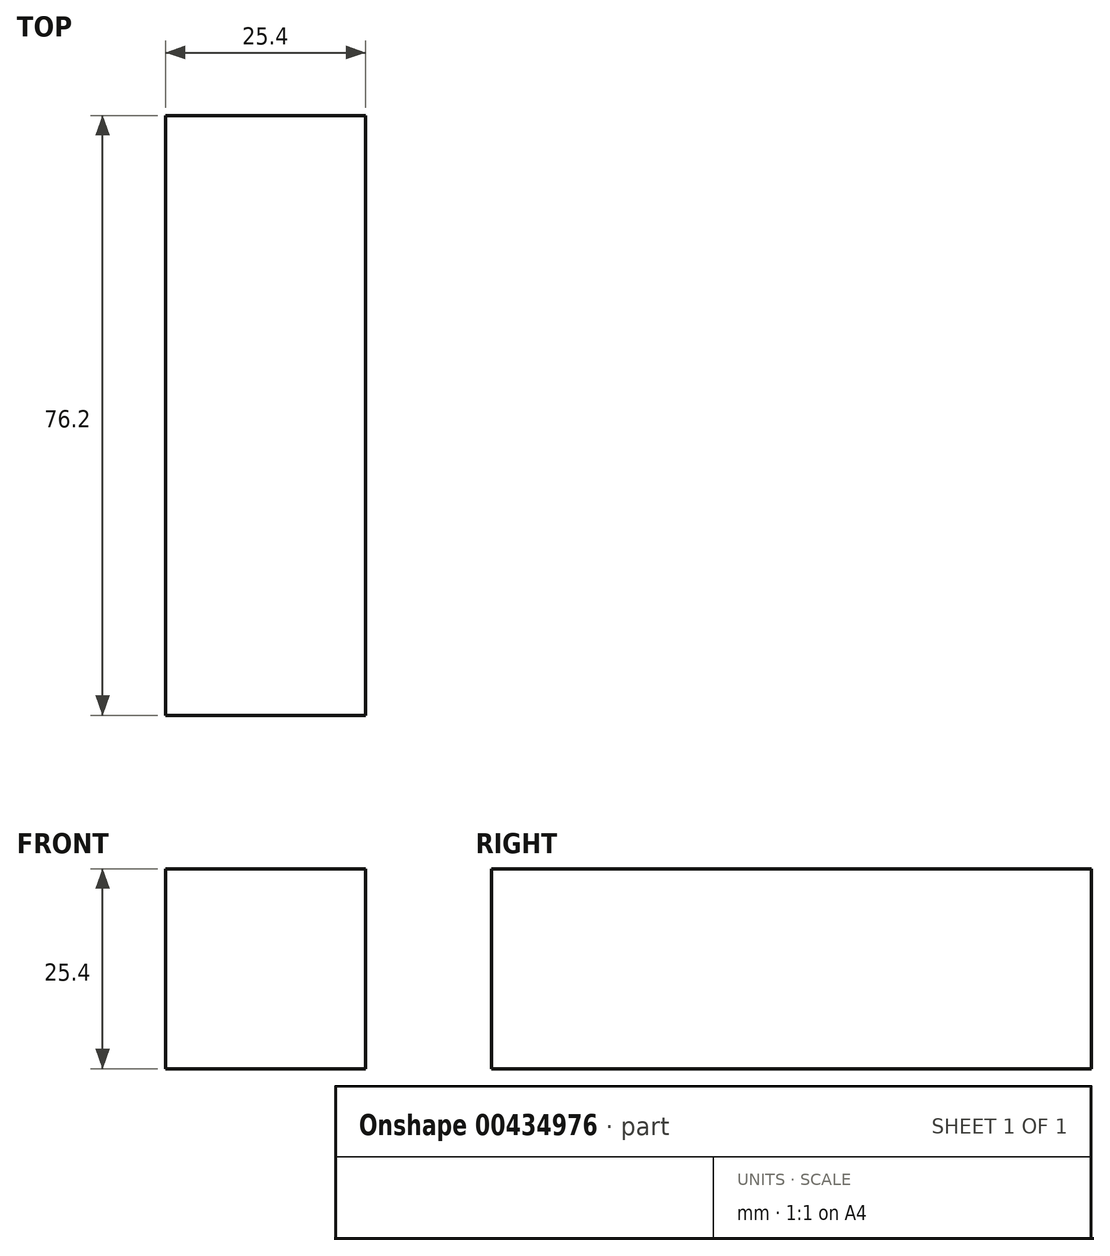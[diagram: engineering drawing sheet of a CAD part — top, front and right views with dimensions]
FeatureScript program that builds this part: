
annotation { "Feature Type Name" : "Feature", "Feature Type Description" : "" }
export const myFeature = defineFeature(function(context is Context, id is Id, definition is map)
    precondition{}
    {
        {
            var Q0;
            Q0=qCreatedBy(makeId("Front.planeOp"),FACE);
            var sketch = newSketch(context, id + "F0", { "sketchPlane" : qUnion([Q0])});
            skLineSegment(sketch, "E0", {"start": v(0, 0) * mm, "end": v(-25.4, 0) * mm});
            skLineSegment(sketch, "E1", {"start": v(-25.4, 0) * mm, "end": v(-25.4, 25.4) * mm});
            skLineSegment(sketch, "E2", {"start": v(-25.4, 25.4) * mm, "end": v(0, 25.4) * mm});
            skLineSegment(sketch, "E3", {"start": v(0, 25.4) * mm, "end": v(0, 0) * mm});
            skSolve(sketch);
        }
        {
            var Q0;
            Q0=makeQuery(id+"F0.imprint","IMPRINT",FACE,{"disambiguationData":[TD([[makeQuery(id+"F0.imprint","IMPRINT",EDGE,{"derivedFrom":sQuery(id+"F0.wireOp",EDGE,"E0")}),-1.0]])]});
            extrude(context, id + "F1", {"entities" : qUnion([Q0]), "depth" : 76.2 * mm});
        }
    });
